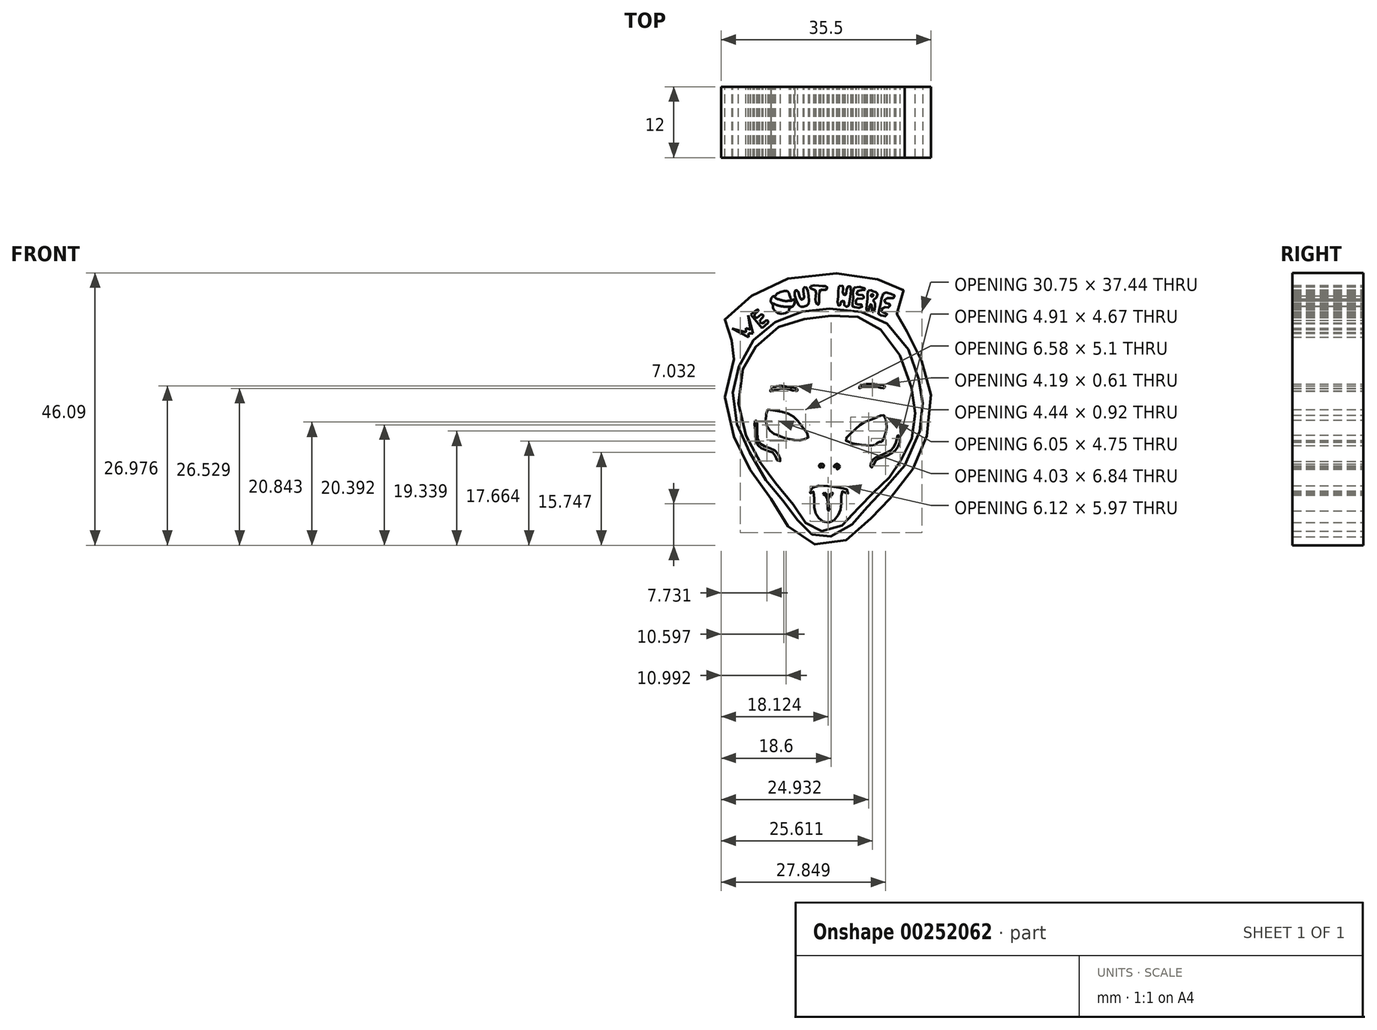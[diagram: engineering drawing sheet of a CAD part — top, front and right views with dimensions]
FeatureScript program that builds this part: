
annotation { "Feature Type Name" : "Feature", "Feature Type Description" : "" }
export const myFeature = defineFeature(function(context is Context, id is Id, definition is map)
    precondition{}
    {
        {
            var Q0;
            Q0=qCreatedBy(makeId("Front.planeOp"),FACE);
            var sketch = newSketch(context, id + "F0", { "sketchPlane" : qUnion([Q0])});
            skFitSpline(sketch, "E0", {"points": [v(-47.02, 44.86) * mm, v(-42.18, 47.36) * mm, v(-34.04, 48.7) * mm, v(-27.4, 47.96) * mm, v(-23.06, 46.9) * mm, v(-21.37, 45.86) * mm, v(-21.17, 44.56) * mm, v(-22.36, 41.97) * mm, v(-22.46, 40.47) * mm, v(-21.12, 39.17) * mm, v(-19.72, 37.08) * mm, v(-17.77, 32.74) * mm, v(-16.72, 28.64) * mm, v(-17.07, 22.45) * mm, v(-18.27, 18.36) * mm, v(-20.88, 13.8) * mm, v(-23.85, 10.3) * mm, v(-25.99, 8.4) * mm, v(-27.41, 6.37) * mm, v(-30.67, 3.64) * mm, v(-34.24, 2.64) * mm, v(-37.74, 3.23) * mm, v(-40.7, 5.66) * mm, v(-42.3, 8.33) * mm, v(-44.98, 12.2) * mm, v(-47.47, 15.75) * mm, v(-49.55, 19.9) * mm, v(-51.2, 25.48) * mm, v(-51.27, 30.7) * mm, v(-49.43, 35.45) * mm, v(-49.37, 36.76) * mm, v(-50.73, 37.41) * mm, v(-52.16, 38.96) * mm, v(-50.62, 42.04) * mm, v(-47.02, 44.86) * mm]});
            skLineSegment(sketch, "E1", {"start": v(-50.3, 39.32) * mm, "end": v(-47.51, 37.87) * mm});
            skLineSegment(sketch, "E2", {"start": v(-47.51, 37.87) * mm, "end": v(-47.51, 38.49) * mm});
            skLineSegment(sketch, "E3", {"start": v(-47.51, 38.49) * mm, "end": v(-46.75, 38.49) * mm});
            skLineSegment(sketch, "E4", {"start": v(-46.75, 38.49) * mm, "end": v(-47.6, 41.54) * mm});
            skLineSegment(sketch, "E5", {"start": v(-47.6, 41.54) * mm, "end": v(-47.23, 39.14) * mm});
            skLineSegment(sketch, "E6", {"start": v(-47.23, 39.14) * mm, "end": v(-47.99, 39.37) * mm});
            skLineSegment(sketch, "E7", {"start": v(-47.99, 39.37) * mm, "end": v(-47.99, 38.7) * mm});
            skLineSegment(sketch, "E8", {"start": v(-50.3, 39.32) * mm, "end": v(-47.99, 38.7) * mm});
            skLineSegment(sketch, "E9", {"start": v(-47.16, 41.63) * mm, "end": v(-45.27, 39.39) * mm});
            skLineSegment(sketch, "E10", {"start": v(-45.27, 39.39) * mm, "end": v(-44.2, 40.28) * mm});
            skLineSegment(sketch, "E11", {"start": v(-47.16, 41.63) * mm, "end": v(-46.14, 42.49) * mm});
            skFitSpline(sketch, "E12", {"points": [v(-46.14, 42.49) * mm, v(-45.9, 42.49) * mm, v(-45.92, 42.24) * mm, v(-46.5, 41.71) * mm, v(-46.45, 41.3) * mm, v(-46.14, 41.13) * mm, v(-45.47, 41.66) * mm, v(-45.1, 41.6) * mm, v(-45.04, 41.38) * mm, v(-45.59, 40.67) * mm, v(-45.57, 40.46) * mm, v(-45.22, 40.16) * mm, v(-44.53, 40.7) * mm, v(-44.23, 40.6) * mm, v(-44.2, 40.28) * mm], "startDerivative": vector(5.34, 1.15) * mm, "endDerivative": vector(-0.72, -5.71) * mm});
            skFitSpline(sketch, "E13", {"points": [v(-39.74, 45.58) * mm, v(-39, 43.25) * mm, v(-38.49, 42.99) * mm, v(-37.54, 43.27) * mm, v(-37.34, 44.3) * mm, v(-37.77, 46.27) * mm, v(-38.15, 46.25) * mm, v(-38.26, 45.76) * mm, v(-38.14, 44.93) * mm, v(-38.17, 44.45) * mm, v(-38.47, 44.19) * mm, v(-38.86, 44.63) * mm, v(-39.21, 45.72) * mm, v(-39.74, 45.58) * mm]});
            skFitSpline(sketch, "E14", {"points": [v(-37, 46.5) * mm, v(-37.1, 46.13) * mm, v(-36.2, 45.76) * mm, v(-36.16, 44.73) * mm, v(-36.14, 43.81) * mm, v(-35.79, 43.3) * mm, v(-35.61, 43.55) * mm, v(-35.58, 44.71) * mm, v(-35.42, 45.76) * mm, v(-35.03, 45.84) * mm, v(-34.45, 45.86) * mm, v(-34.22, 46.2) * mm, v(-34.38, 46.43) * mm, v(-35.28, 46.5) * mm, v(-37, 46.5) * mm]});
            skFitSpline(sketch, "E15", {"points": [v(-32.2, 46.5) * mm, v(-32.33, 44.98) * mm, v(-32.44, 43.48) * mm, v(-32.19, 43.13) * mm, v(-31.96, 43.44) * mm, v(-31.89, 43.85) * mm, v(-31.52, 44) * mm, v(-31.33, 43.85) * mm, v(-31.33, 43.32) * mm, v(-31.22, 43.1) * mm, v(-30.81, 42.97) * mm, v(-30.51, 43.43) * mm, v(-30.32, 44.66) * mm, v(-30.25, 46.25) * mm, v(-30.51, 46.5) * mm, v(-30.9, 46.1) * mm, v(-31, 45.2) * mm, v(-31.27, 44.96) * mm, v(-31.54, 45.16) * mm, v(-31.55, 45.84) * mm, v(-31.55, 46.5) * mm, v(-32.2, 46.5) * mm]});
            skFitSpline(sketch, "E16", {"points": [v(-29.67, 46.25) * mm, v(-29.8, 44.57) * mm, v(-29.93, 43.53) * mm, v(-29.93, 43.04) * mm, v(-29.6, 42.91) * mm, v(-28.68, 42.8) * mm, v(-28.3, 43.04) * mm, v(-28.38, 43.34) * mm, v(-28.94, 43.37) * mm, v(-29.3, 43.4) * mm, v(-29.38, 43.85) * mm, v(-29.23, 44.36) * mm, v(-28.34, 44.34) * mm, v(-28, 44.5) * mm, v(-28.04, 44.87) * mm, v(-28.84, 45) * mm, v(-29.2, 45.05) * mm, v(-29.17, 45.38) * mm, v(-28.84, 45.8) * mm, v(-28.04, 45.76) * mm, v(-27.76, 46.02) * mm, v(-28.03, 46.18) * mm, v(-29.67, 46.25) * mm]});
            skFitSpline(sketch, "E17", {"points": [v(-27.28, 45.74) * mm, v(-27.37, 44.5) * mm, v(-27.57, 42.46) * mm, v(-27.4, 42.17) * mm, v(-27.21, 42.33) * mm, v(-27.02, 43.23) * mm, v(-26.83, 43.4) * mm, v(-26.65, 43.18) * mm, v(-26.67, 42.31) * mm, v(-26.54, 42.05) * mm, v(-26.23, 42.5) * mm, v(-26.12, 43.29) * mm, v(-26.26, 43.85) * mm, v(-26.5, 44) * mm, v(-25.82, 44.64) * mm, v(-25.79, 45.28) * mm, v(-26.31, 45.56) * mm, v(-26.72, 45.74) * mm, v(-27.28, 45.74) * mm]});
            skFitSpline(sketch, "E18", {"points": [v(-26.76, 45.05) * mm, v(-26.8, 44.77) * mm, v(-26.53, 44.75) * mm, v(-26.44, 44.98) * mm, v(-26.5, 45.1) * mm, v(-26.76, 45.05) * mm]});
            skFitSpline(sketch, "E19", {"points": [v(-24.73, 45.23) * mm, v(-25.11, 43.83) * mm, v(-25.26, 43.04) * mm, v(-25.57, 41.73) * mm, v(-25.17, 41.52) * mm, v(-24.29, 41.4) * mm, v(-24.07, 41.71) * mm, v(-24.5, 41.93) * mm, v(-24.9, 42.05) * mm, v(-25.06, 42.31) * mm, v(-24.87, 42.77) * mm, v(-24.3, 42.91) * mm, v(-23.88, 42.84) * mm, v(-23.61, 43.1) * mm, v(-23.6, 43.32) * mm, v(-23.83, 43.5) * mm, v(-24.29, 43.59) * mm, v(-24.57, 43.96) * mm, v(-24.3, 44.36) * mm, v(-23.67, 44.47) * mm, v(-23.17, 44.38) * mm, v(-22.94, 44.56) * mm, v(-22.86, 44.9) * mm, v(-23.3, 45.14) * mm, v(-24.36, 45.4) * mm, v(-24.73, 45.23) * mm]});
            skFitSpline(sketch, "E20", {"points": [v(-38.42, 42.18) * mm, v(-34.33, 42.66) * mm, v(-28.51, 42.12) * mm, v(-24.42, 40.4) * mm, v(-20.32, 35.47) * mm, v(-18.66, 30.43) * mm, v(-18.13, 27.1) * mm, v(-18.25, 23.2) * mm, v(-21.1, 16.13) * mm, v(-24.54, 12.21) * mm, v(-27.21, 9.39) * mm, v(-29.02, 7.3) * mm, v(-31.59, 4.77) * mm, v(-34.65, 4.06) * mm, v(-36.41, 4.27) * mm, v(-38.22, 5.61) * mm, v(-39.7, 7.54) * mm, v(-42.12, 10.65) * mm, v(-44.64, 13.67) * mm, v(-47.53, 18.7) * mm, v(-49.63, 23.66) * mm, v(-50.18, 29.24) * mm, v(-49.08, 33.1) * mm, v(-46.44, 37.63) * mm, v(-42.92, 40.44) * mm, v(-38.42, 42.18) * mm]});
            skFitSpline(sketch, "E21", {"points": [v(-38.13, 40.89) * mm, v(-33.84, 41.44) * mm, v(-29.6, 41.39) * mm, v(-26.05, 39.84) * mm, v(-22.4, 35.7) * mm, v(-19.96, 29.26) * mm, v(-19.36, 25.32) * mm, v(-19.71, 21.43) * mm, v(-20.76, 18.53) * mm, v(-22.96, 15.29) * mm, v(-23.9, 13.89) * mm, v(-26, 11.84) * mm, v(-27.6, 10.4) * mm, v(-30, 7.7) * mm, v(-32.24, 5.66) * mm, v(-34.93, 5) * mm, v(-36.43, 5.3) * mm, v(-38.48, 7.1) * mm, v(-39.92, 9.5) * mm, v(-42.77, 12.94) * mm, v(-44.96, 15.79) * mm, v(-47.66, 20.53) * mm, v(-49.26, 26.62) * mm, v(-48.2, 33.2) * mm, v(-46.26, 36.3) * mm, v(-42.12, 39.74) * mm, v(-38.13, 40.89) * mm]});
            skFitSpline(sketch, "E22", {"points": [v(-37.1, 11.76) * mm, v(-36.48, 12.5) * mm, v(-33.19, 12.5) * mm, v(-31.2, 12.16) * mm, v(-30.74, 11.88) * mm, v(-30.77, 11.26) * mm, v(-31.42, 11.76) * mm, v(-31.7, 11.66) * mm, v(-31.87, 9.59) * mm, v(-32.22, 8.02) * mm, v(-33.38, 6.65) * mm, v(-34.98, 6.71) * mm, v(-35.93, 7.63) * mm, v(-36.44, 9.3) * mm, v(-36.64, 11.76) * mm, v(-37.15, 11.4) * mm, v(-37.1, 11.76) * mm]});
            skFitSpline(sketch, "E23", {"points": [v(-34.66, 11.55) * mm, v(-34.03, 11.13) * mm, v(-33.35, 11.55) * mm, v(-33.38, 11.13) * mm, v(-34, 10.72) * mm, v(-33.91, 8.52) * mm, v(-34.06, 8.55) * mm, v(-34.36, 10.87) * mm, v(-34.9, 11.28) * mm, v(-34.66, 11.55) * mm]});
            skFitSpline(sketch, "E24", {"points": [v(-35.3, 15.77) * mm, v(-35.3, 15.96) * mm, v(-35.12, 16.01) * mm, v(-34.94, 15.78) * mm, v(-34.8, 15.99) * mm, v(-34.9, 16.32) * mm, v(-35.4, 16.33) * mm, v(-35.6, 15.97) * mm, v(-35.3, 15.77) * mm]});
            skFitSpline(sketch, "E25", {"points": [v(-33.04, 16.05) * mm, v(-32.79, 16.3) * mm, v(-32.53, 16.38) * mm, v(-32.17, 16.12) * mm, v(-32.22, 15.66) * mm, v(-32.59, 15.51) * mm, v(-32.56, 15.77) * mm, v(-32.54, 16.03) * mm, v(-32.82, 16) * mm, v(-32.98, 15.87) * mm, v(-33.1, 15.9) * mm, v(-33.04, 16.05) * mm]});
            skFitSpline(sketch, "E26", {"points": [v(-46.46, 23.7) * mm, v(-46.44, 22.53) * mm, v(-46.32, 20.5) * mm, v(-45.79, 19.38) * mm, v(-44.91, 18.85) * mm, v(-44, 18.53) * mm, v(-43.23, 18.13) * mm, v(-42.64, 16.98) * mm, v(-42.14, 16.9) * mm, v(-42.24, 17.38) * mm, v(-43, 18.64) * mm, v(-44.62, 19.28) * mm, v(-45.87, 20.3) * mm, v(-46.07, 23.05) * mm, v(-46.2, 23.76) * mm, v(-46.46, 23.7) * mm]});
            skFitSpline(sketch, "E27", {"points": [v(-25.32, 17.77) * mm, v(-24.26, 18.28) * mm, v(-23.13, 18.98) * mm, v(-22.43, 20.68) * mm, v(-22.23, 21.26) * mm, v(-21.87, 20.53) * mm, v(-22.44, 19.02) * mm, v(-23.56, 18.06) * mm, v(-25.54, 17.26) * mm, v(-26.09, 16.85) * mm, v(-26.58, 15.83) * mm, v(-26.83, 15.86) * mm, v(-26.87, 16.37) * mm, v(-26.3, 17.32) * mm, v(-25.32, 17.77) * mm]});
            skFitSpline(sketch, "E28", {"points": [v(-30.26, 21.53) * mm, v(-28.17, 23.31) * mm, v(-27.03, 23.8) * mm, v(-25.5, 24.45) * mm, v(-24.61, 24.59) * mm, v(-24.25, 23.41) * mm, v(-24.25, 21.96) * mm, v(-25.02, 20.13) * mm, v(-25.44, 20.11) * mm, v(-25.84, 19.84) * mm, v(-26.42, 19.54) * mm, v(-31.07, 20.32) * mm, v(-30.26, 21.53) * mm]});
            skFitSpline(sketch, "E29", {"points": [v(-44.31, 25.56) * mm, v(-43.96, 25.57) * mm, v(-42.14, 25.3) * mm, v(-40.04, 24.47) * mm, v(-38.91, 23.31) * mm, v(-38.7, 22.96) * mm, v(-37.37, 21.08) * mm, v(-37.9, 20.6) * mm, v(-39.32, 20.4) * mm, v(-41.05, 20.72) * mm, v(-41.46, 20.83) * mm, v(-42.72, 21.3) * mm, v(-43.1, 21.4) * mm, v(-44.14, 22.28) * mm, v(-44.63, 24.05) * mm, v(-44.31, 25.56) * mm]});
            skFitSpline(sketch, "E30", {"points": [v(-43.3, 29.3) * mm, v(-41.88, 29.6) * mm, v(-40.3, 29.32) * mm, v(-39.38, 29.14) * mm, v(-39.27, 28.79) * mm, v(-40.59, 28.99) * mm, v(-41.56, 29.14) * mm, v(-42.87, 28.91) * mm, v(-43.9, 28.72) * mm, v(-43.3, 29.3) * mm]});
            skFitSpline(sketch, "E31", {"points": [v(-26.2, 29.9) * mm, v(-25.12, 29.78) * mm, v(-24.53, 29.65) * mm, v(-24.55, 29.25) * mm, v(-26.39, 29.53) * mm, v(-28.24, 29.43) * mm, v(-28.83, 29.21) * mm, v(-28.69, 29.5) * mm, v(-27.74, 29.88) * mm, v(-26.2, 29.9) * mm]});
            skFitSpline(sketch, "E32", {"points": [v(-43.07, 44.76) * mm, v(-42.87, 45) * mm, v(-42.6, 45.26) * mm, v(-41.73, 45.57) * mm, v(-40.83, 45.51) * mm, v(-40.26, 44.16) * mm, v(-39.83, 44.16) * mm, v(-39.77, 43.54) * mm, v(-40.3, 42.89) * mm, v(-40.6, 42.74) * mm, v(-40.68, 42.37) * mm, v(-41.05, 42.01) * mm, v(-42.07, 41.8) * mm, v(-42.89, 42.1) * mm, v(-43.42, 42.87) * mm, v(-43.4, 43.32) * mm, v(-43.74, 43.78) * mm, v(-43.57, 44.58) * mm, v(-43.25, 44.79) * mm, v(-43.07, 44.76) * mm]});
            skFitSpline(sketch, "E33", {"points": [v(-42.83, 44.75) * mm, v(-42.45, 45.12) * mm, v(-41.52, 45.4) * mm, v(-40.99, 45.3) * mm, v(-40.75, 44.75) * mm, v(-40.45, 43.99) * mm, v(-39.83, 44.16) * mm, v(-39.75, 43.68) * mm, v(-40.15, 43.04) * mm, v(-40.6, 43.01) * mm, v(-40.79, 42.81) * mm, v(-40.9, 42.41) * mm, v(-41.2, 42.13) * mm, v(-41.85, 42) * mm, v(-42.03, 41.98) * mm, v(-42.62, 42.17) * mm, v(-42.98, 42.46) * mm, v(-43.18, 42.89) * mm, v(-43.1, 43.43) * mm, v(-43.6, 43.6) * mm, v(-43.73, 44.25) * mm, v(-43.25, 44.79) * mm, v(-42.98, 44.45) * mm, v(-42.83, 44.75) * mm]});
            skFitSpline(sketch, "E34", {"points": [v(-42.98, 44.45) * mm, v(-41.7, 44.02) * mm, v(-41.19, 43.97) * mm, v(-40.37, 43.98) * mm], "startDerivative": vector(3.45, -1.28) * mm, "endDerivative": vector(2.73, 0.02) * mm});
            skFitSpline(sketch, "E35", {"points": [v(-43.1, 43.43) * mm, v(-42, 43.07) * mm, v(-40.6, 43.01) * mm], "startDerivative": vector(2.2, -0.91) * mm, "endDerivative": vector(2.78, 0.07) * mm});
            skSolve(sketch);
        }
        {
            var Q0;
            Q0=makeQuery(id+"F0.imprint","IMPRINT",FACE,{"disambiguationData":[TD([[makeQuery(id+"F0.imprint","IMPRINT",EDGE,{"derivedFrom":sQuery(id+"F0.wireOp",EDGE,"E0")}),-1.0]])]});
            var Q1;
            {var subQ0=sQuery(id+"F0.wireOp",EDGE,"2b3a6fc7-aa35-4c7c-b997-2844fceb4e02");var subQ1=sQuery(id+"F0.wireOp",EDGE,"80aa8a0d-d0ad-4b13-a698-77e9bd98780b");var subQ2=makeQuery(id+"F0.imprint","INTERSECT",VERTEX,{"disambiguationData":[OD(1.0)],"derivedFrom":[subQ1,subQ0]});Q1=makeQuery(id+"F0.imprint","IMPRINT",FACE,{"disambiguationData":[TD([[makeQuery(id+"F0.imprint","IMPRINT",EDGE,{"disambiguationData":[TD([[subQ2,1.0]])],"derivedFrom":subQ1}),1.0]])]});}
            var Q2;
            {var subQ0=sQuery(id+"F0.wireOp",EDGE,"2b3a6fc7-aa35-4c7c-b997-2844fceb4e02");var subQ1=sQuery(id+"F0.wireOp",EDGE,"80aa8a0d-d0ad-4b13-a698-77e9bd98780b");var subQ2=makeQuery(id+"F0.imprint","INTERSECT",VERTEX,{"disambiguationData":[OD(3.0)],"derivedFrom":[subQ1,subQ0]});Q2=makeQuery(id+"F0.imprint","IMPRINT",FACE,{"disambiguationData":[TD([[makeQuery(id+"F0.imprint","IMPRINT",EDGE,{"disambiguationData":[TD([[subQ2,-1.0]])],"derivedFrom":subQ1}),-1.0]])]});}
            var Q3;
            {var subQ0=sQuery(id+"F0.wireOp",EDGE,"2b3a6fc7-aa35-4c7c-b997-2844fceb4e02");var subQ1=sQuery(id+"F0.wireOp",EDGE,"80aa8a0d-d0ad-4b13-a698-77e9bd98780b");var subQ2=makeQuery(id+"F0.imprint","INTERSECT",VERTEX,{"disambiguationData":[OD(0.0)],"derivedFrom":[subQ1,subQ0]});Q3=makeQuery(id+"F0.imprint","IMPRINT",FACE,{"disambiguationData":[TD([[makeQuery(id+"F0.imprint","IMPRINT",EDGE,{"disambiguationData":[TD([[subQ2,-1.0]])],"derivedFrom":subQ1}),1.0]])]});}
            var Q4;
            Q4=makeQuery(id+"F0.imprint","IMPRINT",FACE,{"disambiguationData":[TD([[makeQuery(id+"F0.imprint","IMPRINT",EDGE,{"derivedFrom":sQuery(id+"F0.wireOp",EDGE,"E18")}),1.0]])]});
            var Q5;
            Q5=makeQuery(id+"F0.imprint","IMPRINT",FACE,{"disambiguationData":[TD([[makeQuery(id+"F0.imprint","IMPRINT",EDGE,{"derivedFrom":sQuery(id+"F0.wireOp",EDGE,"AFMhThZB-HP6E-V7qj-hnUd-QaNlzZNTURHN")}),1.0]])]});
            var Q6;
            Q6=makeQuery(id+"F0.imprint","IMPRINT",FACE,{"disambiguationData":[TD([[makeQuery(id+"F0.imprint","IMPRINT",EDGE,{"derivedFrom":sQuery(id+"F0.wireOp",EDGE,"oracrgsL-PgKi-cfWO-B6q8-xcAS3gdlpo5W")}),1.0]])]});
            var Q7;
            Q7=makeQuery(id+"F0.imprint","IMPRINT",FACE,{"disambiguationData":[TD([[makeQuery(id+"F0.imprint","IMPRINT",EDGE,{"derivedFrom":sQuery(id+"F0.wireOp",EDGE,"gOLJmPyi-1Rtu-gi4K-BdgX-iHq6hCuFCN8P")}),1.0]])]});
            var Q8;
            Q8=makeQuery(id+"F0.imprint","IMPRINT",FACE,{"disambiguationData":[TD([[makeQuery(id+"F0.imprint","IMPRINT",EDGE,{"derivedFrom":sQuery(id+"F0.wireOp",EDGE,"Bh1o2fMj-yvNN-QOv9-EIoX-i9nIM8NS1zfd")}),1.0]])]});
            var Q9;
            Q9=makeQuery(id+"F0.imprint","IMPRINT",FACE,{"disambiguationData":[TD([[makeQuery(id+"F0.imprint","IMPRINT",EDGE,{"derivedFrom":sQuery(id+"F0.wireOp",EDGE,"K7vmnW2C-Q84v-tune-eKCZ-ALzPXEr5asnx")}),1.0]])]});
            var Q10;
            Q10=makeQuery(id+"F0.imprint","IMPRINT",FACE,{"disambiguationData":[TD([[makeQuery(id+"F0.imprint","IMPRINT",EDGE,{"derivedFrom":sQuery(id+"F0.wireOp",EDGE,"E21")}),-1.0]])]});
            var Q11;
            Q11=makeQuery(id+"F0.imprint","IMPRINT",FACE,{"disambiguationData":[TD([[makeQuery(id+"F0.imprint","IMPRINT",EDGE,{"derivedFrom":sQuery(id+"F0.wireOp",EDGE,"E23")}),-1.0]])]});
            var Q12;
            {var subQ0=sQuery(id+"F0.wireOp",EDGE,"b1ef19d1-d852-480b-8519-57bfa002098d");Q12=makeQuery(id+"F0.imprint","IMPRINT",FACE,{"disambiguationData":[TD([[makeQuery(id+"F0.imprint","IMPRINT",EDGE,{"derivedFrom":subQ0}),1.0]])]});}
            var Q13;
            {var subQ0=sQuery(id+"F0.wireOp",EDGE,"E34");Q13=makeQuery(id+"F0.imprint","IMPRINT",FACE,{"disambiguationData":[TD([[makeQuery(id+"F0.imprint","IMPRINT",EDGE,{"derivedFrom":subQ0}),-1.0]])]});}
            var Q14;
            {var subQ0=sQuery(id+"F0.wireOp",EDGE,"E35");Q14=makeQuery(id+"F0.imprint","IMPRINT",FACE,{"disambiguationData":[TD([[makeQuery(id+"F0.imprint","IMPRINT",EDGE,{"derivedFrom":subQ0}),1.0]])]});}
            extrude(context, id + "F1", {"entities" : qUnion([Q0, Q1, Q2, Q3, Q4, Q5, Q6, Q7, Q8, Q9, Q10, Q11, Q12, Q13, Q14]), "depth" : 12 * mm, "offsetDistance" : 25 * mm});
        }
    });
